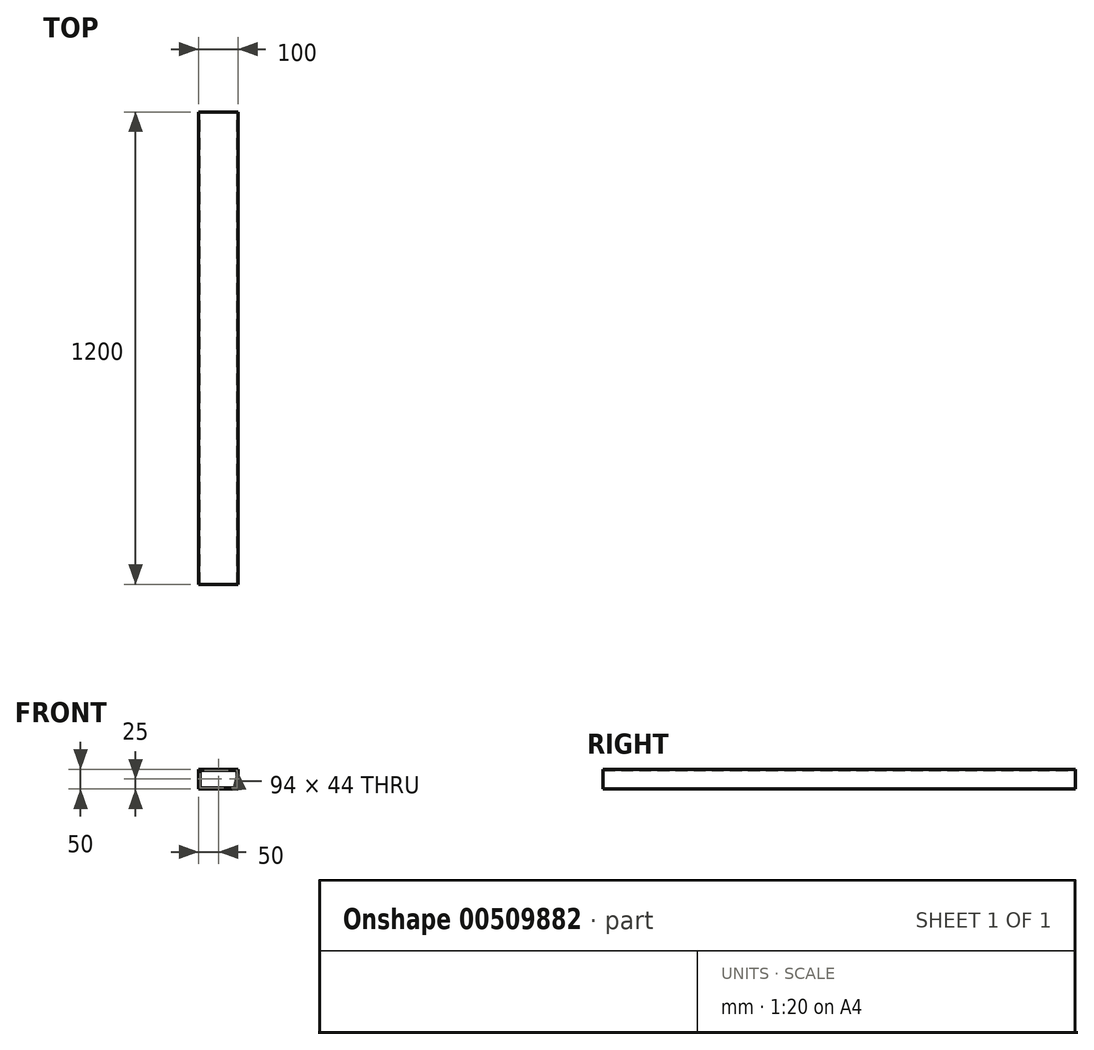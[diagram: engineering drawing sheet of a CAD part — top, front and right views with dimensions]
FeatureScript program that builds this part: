
annotation { "Feature Type Name" : "Feature", "Feature Type Description" : "" }
export const myFeature = defineFeature(function(context is Context, id is Id, definition is map)
    precondition{}
    {
        {
            var Q0;
            Q0=qCreatedBy(makeId("Front.planeOp"),FACE);
            var sketch = newSketch(context, id + "F0", { "sketchPlane" : qUnion([Q0])});
            skLineSegment(sketch, "E0.bottom", {"start": v(50, -25) * mm, "end": v(-50, -25) * mm});
            skLineSegment(sketch, "E0.top", {"start": v(50, 25) * mm, "end": v(-50, 25) * mm});
            skLineSegment(sketch, "E0.left", {"start": v(50, -25) * mm, "end": v(50, 25) * mm});
            skLineSegment(sketch, "E0.right", {"start": v(-50, -25) * mm, "end": v(-50, 25) * mm});
            skPoint(sketch, "E0.middle", {"position": v(0, 0) * mm});
            skLineSegment(sketch, "E1.bottom", {"start": v(47, -22) * mm, "end": v(-47, -22) * mm});
            skLineSegment(sketch, "E1.top", {"start": v(47, 22) * mm, "end": v(-47, 22) * mm});
            skLineSegment(sketch, "E1.left", {"start": v(47, -22) * mm, "end": v(47, 22) * mm});
            skLineSegment(sketch, "E1.right", {"start": v(-47, -22) * mm, "end": v(-47, 22) * mm});
            skSolve(sketch);
        }
        {
            var Q0;
            Q0=makeQuery(id+"F0.imprint","IMPRINT",FACE,{"disambiguationData":[TD([[makeQuery(id+"F0.imprint","IMPRINT",EDGE,{"derivedFrom":sQuery(id+"F0.wireOp",EDGE,"E0.bottom")}),-1.0]])]});
            extrude(context, id + "F1", {"entities" : qUnion([Q0]), "depth" : 1200 * mm, "offsetDistance" : 25 * mm});
        }
    });
